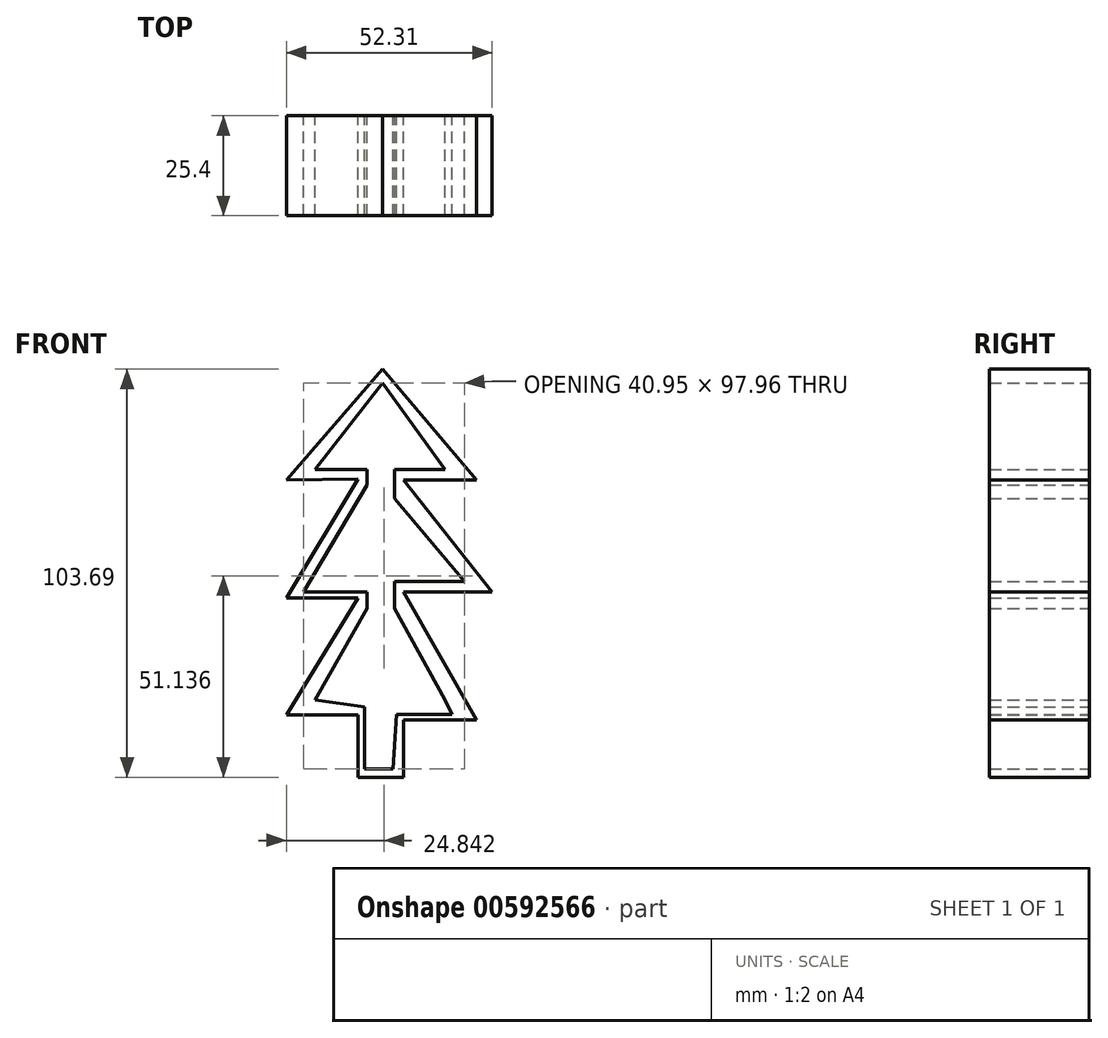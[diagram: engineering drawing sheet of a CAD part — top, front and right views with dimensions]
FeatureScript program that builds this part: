
annotation { "Feature Type Name" : "Feature", "Feature Type Description" : "" }
export const myFeature = defineFeature(function(context is Context, id is Id, definition is map)
    precondition{}
    {
        {
            var Q0;
            Q0=qCreatedBy(makeId("Front.planeOp"),FACE);
            var sketch = newSketch(context, id + "F0", { "sketchPlane" : qUnion([Q0])});
            skLineSegment(sketch, "E0", {"start": v(-13.93, -34.67) * mm, "end": v(-13.93, -54.47) * mm});
            skLineSegment(sketch, "E1", {"start": v(-13.93, -54.47) * mm, "end": v(0, -54.47) * mm});
            skLineSegment(sketch, "E2", {"start": v(0, -54.47) * mm, "end": v(0, -34.05) * mm});
            skLineSegment(sketch, "E3", {"start": v(0, -34.05) * mm, "end": v(13, -34.05) * mm});
            skLineSegment(sketch, "E4", {"start": v(-13.93, -34.67) * mm, "end": v(-29.4, -34.67) * mm});
            skLineSegment(sketch, "E5", {"start": v(-29.4, -34.67) * mm, "end": v(-13.93, -10.83) * mm});
            skLineSegment(sketch, "E6", {"start": v(13, -34.05) * mm, "end": v(0, -9.9) * mm});
            skLineSegment(sketch, "E7", {"start": v(-13.93, -10.83) * mm, "end": v(-34.67, -9.9) * mm});
            skLineSegment(sketch, "E8", {"start": v(-34.67, -9.9) * mm, "end": v(-8.98, 19.8) * mm});
            skLineSegment(sketch, "E9", {"start": v(0, -9.9) * mm, "end": v(19.5, -10.83) * mm});
            skLineSegment(sketch, "E10", {"start": v(19.5, -10.83) * mm, "end": v(0, 19.5) * mm});
            skLineSegment(sketch, "E11", {"start": v(-8.98, 19.8) * mm, "end": v(-25.38, 19.8) * mm});
            skLineSegment(sketch, "E12", {"start": v(-25.38, 19.8) * mm, "end": v(-6.5, 39.93) * mm});
            skLineSegment(sketch, "E13", {"start": v(0, 19.5) * mm, "end": v(13, 19.5) * mm});
            skLineSegment(sketch, "E14", {"start": v(13, 19.5) * mm, "end": v(-6.5, 39.93) * mm});
            skLineSegment(sketch, "E15", {"start": v(-11.35, 31.08) * mm, "end": v(-20.97, 22.11) * mm});
            skLineSegment(sketch, "E16", {"start": v(-20.97, 22.11) * mm, "end": v(-7.84, 22.11) * mm});
            skLineSegment(sketch, "E17", {"start": v(-7.84, 22.11) * mm, "end": v(-7.84, 19.5) * mm});
            skLineSegment(sketch, "E18", {"start": v(-7.84, 19.5) * mm, "end": v(-29.4, -7.14) * mm});
            skLineSegment(sketch, "E19", {"start": v(-29.4, -7.14) * mm, "end": v(-11.41, -7.94) * mm});
            skLineSegment(sketch, "E20", {"start": v(-11.41, -7.94) * mm, "end": v(-11.41, -13.36) * mm});
            skLineSegment(sketch, "E21", {"start": v(-11.41, -13.36) * mm, "end": v(-23.47, -31.37) * mm});
            skLineSegment(sketch, "E22", {"start": v(-23.47, -31.37) * mm, "end": v(-11.41, -31.9) * mm});
            skLineSegment(sketch, "E23", {"start": v(-11.41, -31.9) * mm, "end": v(-11.41, -50.76) * mm});
            skLineSegment(sketch, "E24", {"start": v(-11.41, -50.76) * mm, "end": v(-4, -51.1) * mm});
            skLineSegment(sketch, "E25", {"start": v(-4, -51.1) * mm, "end": v(-4, -32.19) * mm});
            skLineSegment(sketch, "E26", {"start": v(-4, -32.19) * mm, "end": v(8.05, -32.19) * mm});
            skLineSegment(sketch, "E27", {"start": v(8.05, -32.19) * mm, "end": v(-2.33, -12.92) * mm});
            skLineSegment(sketch, "E28", {"start": v(-2.33, -12.92) * mm, "end": v(-2.33, -6.8) * mm});
            skLineSegment(sketch, "E29", {"start": v(-2.33, -6.8) * mm, "end": v(13, -6.8) * mm});
            skLineSegment(sketch, "E30", {"start": v(13, -6.8) * mm, "end": v(-2.7, 17.62) * mm});
            skLineSegment(sketch, "E31", {"start": v(-2.7, 17.62) * mm, "end": v(-2.7, 22.52) * mm});
            skLineSegment(sketch, "E32", {"start": v(-2.7, 22.52) * mm, "end": v(6.78, 22.52) * mm});
            skLineSegment(sketch, "E33", {"start": v(6.78, 22.52) * mm, "end": v(-6.34, 36.27) * mm});
            skLineSegment(sketch, "E34", {"start": v(-6.34, 36.27) * mm, "end": v(-11.35, 31.08) * mm});
            skSolve(sketch);
        }
        {
            var Q0;
            Q0 = qSketchRegion(id + "F0", true);
            extrude(context, id + "F1", {"entities" : qUnion([Q0]), "depth" : 25.4 * mm, "offsetDistance" : 25.4 * mm});
        }
        {
            var Q0;
            Q0=makeQuery(id+"F1.opExtrude","SWEPT_BODY",BODY,{"disambiguationData":[OSD([sQuery(id+"F0.wireOp",EDGE,"E0"),sQuery(id+"F0.wireOp",EDGE,"E1"),sQuery(id+"F0.wireOp",EDGE,"E2"),sQuery(id+"F0.wireOp",EDGE,"E3"),sQuery(id+"F0.wireOp",EDGE,"E4"),sQuery(id+"F0.wireOp",EDGE,"E5"),sQuery(id+"F0.wireOp",EDGE,"E6"),sQuery(id+"F0.wireOp",EDGE,"E7"),sQuery(id+"F0.wireOp",EDGE,"E8"),sQuery(id+"F0.wireOp",EDGE,"E9"),sQuery(id+"F0.wireOp",EDGE,"E10"),sQuery(id+"F0.wireOp",EDGE,"E11"),sQuery(id+"F0.wireOp",EDGE,"E12"),sQuery(id+"F0.wireOp",EDGE,"E13"),sQuery(id+"F0.wireOp",EDGE,"E14"),sQuery(id+"F0.wireOp",EDGE,"E15"),sQuery(id+"F0.wireOp",EDGE,"E16"),sQuery(id+"F0.wireOp",EDGE,"E17"),sQuery(id+"F0.wireOp",EDGE,"E18"),sQuery(id+"F0.wireOp",EDGE,"E19"),sQuery(id+"F0.wireOp",EDGE,"E20"),sQuery(id+"F0.wireOp",EDGE,"E21"),sQuery(id+"F0.wireOp",EDGE,"E22"),sQuery(id+"F0.wireOp",EDGE,"E23"),sQuery(id+"F0.wireOp",EDGE,"E24"),sQuery(id+"F0.wireOp",EDGE,"E25"),sQuery(id+"F0.wireOp",EDGE,"E26"),sQuery(id+"F0.wireOp",EDGE,"E27"),sQuery(id+"F0.wireOp",EDGE,"E28"),sQuery(id+"F0.wireOp",EDGE,"E29"),sQuery(id+"F0.wireOp",EDGE,"E30"),sQuery(id+"F0.wireOp",EDGE,"E31"),sQuery(id+"F0.wireOp",EDGE,"E32"),sQuery(id+"F0.wireOp",EDGE,"E33"),sQuery(id+"F0.wireOp",EDGE,"E34")])]});
            deleteBodies(context, id + "F2", {"entities" : qUnion([Q0])});
        }
        {
            var Q0;
            Q0=qCreatedBy(makeId("Front.planeOp"),FACE);
            var sketch = newSketch(context, id + "F3", { "sketchPlane" : qUnion([Q0])});
            skLineSegment(sketch, "E35", {"start": v(-6.2, -40.55) * mm, "end": v(-6.2, -56.33) * mm});
            skLineSegment(sketch, "E36", {"start": v(-6.2, -56.33) * mm, "end": v(5.26, -56.33) * mm});
            skLineSegment(sketch, "E37", {"start": v(5.26, -56.33) * mm, "end": v(5.26, -41.78) * mm});
            skLineSegment(sketch, "E38", {"start": v(-6.2, -40.55) * mm, "end": v(-24.45, -40.55) * mm});
            skLineSegment(sketch, "E39", {"start": v(5.26, -41.78) * mm, "end": v(23.83, -41.78) * mm});
            skLineSegment(sketch, "E40", {"start": v(23.83, -41.78) * mm, "end": v(5.26, -9.29) * mm});
            skLineSegment(sketch, "E41", {"start": v(-24.45, -40.55) * mm, "end": v(-6.2, -10.83) * mm});
            skLineSegment(sketch, "E42", {"start": v(-6.2, -10.83) * mm, "end": v(-24.45, -10.83) * mm});
            skLineSegment(sketch, "E43", {"start": v(-24.45, -10.83) * mm, "end": v(-6.2, 19.5) * mm});
            skLineSegment(sketch, "E44", {"start": v(5.26, -9.29) * mm, "end": v(27.86, -9.29) * mm});
            skLineSegment(sketch, "E45", {"start": v(27.86, -9.29) * mm, "end": v(5.26, 19.2) * mm});
            skLineSegment(sketch, "E46", {"start": v(-6.2, 19.5) * mm, "end": v(-24.45, 19.2) * mm});
            skLineSegment(sketch, "E47", {"start": v(-24.45, 19.2) * mm, "end": v(0, 47.36) * mm});
            skLineSegment(sketch, "E48", {"start": v(5.26, 19.2) * mm, "end": v(23.83, 19.2) * mm});
            skLineSegment(sketch, "E49", {"start": v(23.83, 19.2) * mm, "end": v(0, 47.36) * mm});
            skLineSegment(sketch, "E50", {"start": v(0, 43.78) * mm, "end": v(-17.12, 21.9) * mm});
            skLineSegment(sketch, "E51", {"start": v(-17.12, 21.9) * mm, "end": v(-3.95, 21.9) * mm});
            skLineSegment(sketch, "E52", {"start": v(-3.95, 21.9) * mm, "end": v(-3.95, 17.94) * mm});
            skLineSegment(sketch, "E53", {"start": v(-3.95, 17.94) * mm, "end": v(-20.08, -9.29) * mm});
            skLineSegment(sketch, "E54", {"start": v(-20.08, -9.29) * mm, "end": v(-3.95, -9.29) * mm});
            skLineSegment(sketch, "E55", {"start": v(-3.95, -9.29) * mm, "end": v(-3.95, -13.5) * mm});
            skLineSegment(sketch, "E56", {"start": v(-3.95, -13.5) * mm, "end": v(-17.12, -36.64) * mm});
            skLineSegment(sketch, "E57", {"start": v(0, 43.78) * mm, "end": v(15.9, 21.9) * mm});
            skLineSegment(sketch, "E58", {"start": v(15.9, 21.9) * mm, "end": v(3.05, 21.9) * mm});
            skLineSegment(sketch, "E59", {"start": v(3.05, 21.9) * mm, "end": v(3.05, 14.5) * mm});
            skLineSegment(sketch, "E60", {"start": v(3.05, 14.5) * mm, "end": v(20.87, -6.55) * mm});
            skLineSegment(sketch, "E61", {"start": v(20.87, -6.55) * mm, "end": v(3.05, -6.55) * mm});
            skLineSegment(sketch, "E62", {"start": v(3.05, -6.55) * mm, "end": v(3.05, -13.5) * mm});
            skLineSegment(sketch, "E63", {"start": v(3.05, -13.5) * mm, "end": v(15.9, -36.64) * mm});
            skLineSegment(sketch, "E64", {"start": v(-17.12, -36.64) * mm, "end": v(-4.53, -38.52) * mm});
            skLineSegment(sketch, "E65", {"start": v(-4.53, -38.52) * mm, "end": v(-4.53, -54.17) * mm});
            skLineSegment(sketch, "E66", {"start": v(-4.53, -54.17) * mm, "end": v(2.71, -54.17) * mm});
            skLineSegment(sketch, "E67", {"start": v(2.71, -54.17) * mm, "end": v(3.5, -40.38) * mm});
            skLineSegment(sketch, "E68", {"start": v(3.5, -40.38) * mm, "end": v(17.58, -40.38) * mm});
            skLineSegment(sketch, "E69", {"start": v(15.9, -36.64) * mm, "end": v(17.58, -40.38) * mm});
            skSolve(sketch);
        }
        {
            var Q0;
            Q0 = qSketchRegion(id + "F3", true);
            extrude(context, id + "F4", {"entities" : qUnion([Q0]), "depth" : 25.4 * mm, "offsetDistance" : 25.4 * mm});
        }
    });
